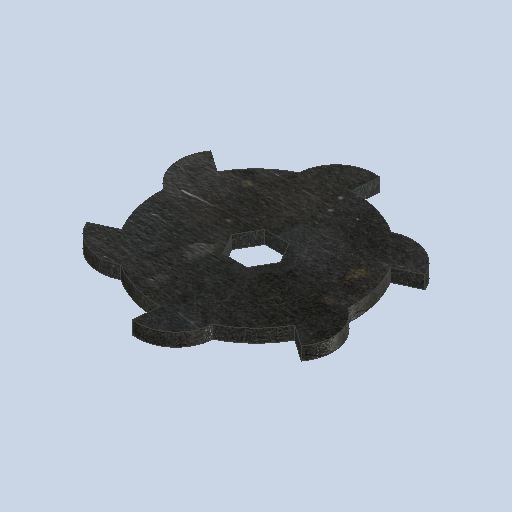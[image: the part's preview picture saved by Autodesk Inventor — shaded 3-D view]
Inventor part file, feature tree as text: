
AUTODESK INVENTOR PART (.ipt)
format: ipt  version: 2025 (Build 290162010, 162A)  size: 261,632 bytes
history: native  units: mm
features: extrude x2, sketch x2, pattern_circular x1, other x1
ambient origin geometry x8: Origin, YZ Plane, XZ Plane, XY Plane, X Axis, Y Axis, Z Axis, Center Point
bodies: Solid1 (feature_tree)
feature tree (6):
  extrude  "Extrusion1"  Depth=32.2mm
  extrude  "Extrusion2"  Depth=30.0mm
  pattern_circular  "Circular Pattern1"  [2 undecoded]
  sketch  "Sketch1"  dims[d0=32.2mm d2=150.0mm]
  sketch  "Sketch2"  dims[d3=10.0mm d4=0.0mm d5=0.872665mm d8=6.108652mm d9=10.0mm d10=0.0mm d11=60.0mm d12=360.0deg d14=30.0mm d15=33.0mm d16=20.0mm]
  other  "Definition1"
note: 2 required parameter values undecoded (feature->parameter linkage not recoverable at this tier; creation-order binding heuristic only, values carry confidence <= 0.55)
